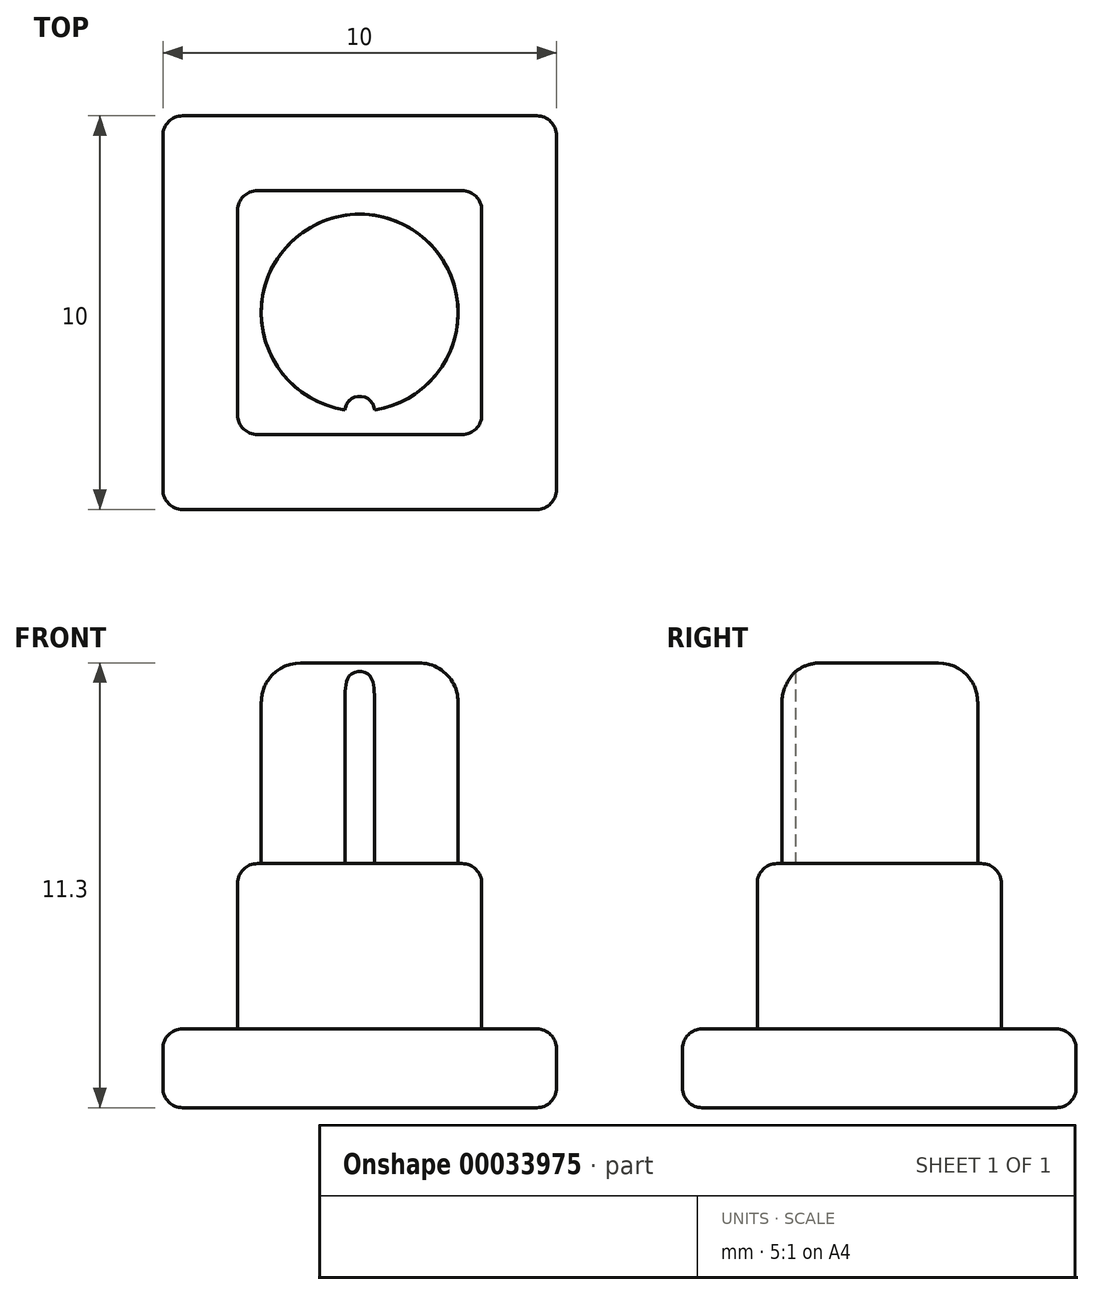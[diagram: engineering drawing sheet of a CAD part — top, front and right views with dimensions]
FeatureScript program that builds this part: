
annotation { "Feature Type Name" : "Feature", "Feature Type Description" : "" }
export const myFeature = defineFeature(function(context is Context, id is Id, definition is map)
    precondition{}
    {
        {
            var Q0;
            Q0=qCreatedBy(makeId("Top.planeOp"),FACE);
            var sketch = newSketch(context, id + "F0", { "sketchPlane" : qUnion([Q0])});
            skLineSegment(sketch, "E0.rect.bottom", {"start": v(3.1, -3.1) * mm, "end": v(-3.1, -3.1) * mm});
            skLineSegment(sketch, "E0.rect.top", {"start": v(3.1, 3.1) * mm, "end": v(-3.1, 3.1) * mm});
            skLineSegment(sketch, "E0.rect.left", {"start": v(3.1, -3.1) * mm, "end": v(3.1, 3.1) * mm});
            skLineSegment(sketch, "E0.rect.right", {"start": v(-3.1, -3.1) * mm, "end": v(-3.1, 3.1) * mm});
            skPoint(sketch, "E0.rect.middle", {"position": v(0, 0) * mm});
            skLineSegment(sketch, "E1.rect.bottom", {"start": v(5, -5) * mm, "end": v(-5, -5) * mm});
            skLineSegment(sketch, "E1.rect.top", {"start": v(5, 5) * mm, "end": v(-5, 5) * mm});
            skLineSegment(sketch, "E1.rect.left", {"start": v(5, -5) * mm, "end": v(5, 5) * mm});
            skLineSegment(sketch, "E1.rect.right", {"start": v(-5, -5) * mm, "end": v(-5, 5) * mm});
            skSolve(sketch);
        }
        {
            var Q0;
            Q0=makeQuery(id+"F0.imprint","IMPRINT",FACE,{"disambiguationData":[TD([[makeQuery(id+"F0.imprint","IMPRINT",EDGE,{"derivedFrom":sQuery(id+"F0.wireOp",EDGE,"E0.rect.bottom")}),-1.0]])]});
            extrude(context, id + "F1", {"entities" : qUnion([Q0]), "depth" : 6.2 * mm});
        }
        {
            var Q0;
            Q0=makeQuery(id+"F0.imprint","IMPRINT",FACE,{"disambiguationData":[TD([[makeQuery(id+"F0.imprint","IMPRINT",EDGE,{"derivedFrom":sQuery(id+"F0.wireOp",EDGE,"E0.rect.bottom")}),1.0]])]});
            var Q1;
            Q1=makeQuery(id+"F0.imprint","IMPRINT",FACE,{"disambiguationData":[TD([[makeQuery(id+"F0.imprint","IMPRINT",EDGE,{"derivedFrom":sQuery(id+"F0.wireOp",EDGE,"E0.rect.bottom")}),-1.0]])]});
            extrude(context, id + "F2", {"entities" : qUnion([Q0, Q1]), "operationType" : NewBodyOperationType.ADD, "depth" : 2 * mm});
        }
        {
            var Q0;
            Q0=makeQuery(id+"F1.opExtrude","CAP_FACE",FACE,{"disambiguationData":[OSD([sQuery(id+"F0.wireOp",EDGE,"E0.rect.bottom"),sQuery(id+"F0.wireOp",EDGE,"E0.rect.top"),sQuery(id+"F0.wireOp",EDGE,"E0.rect.left"),sQuery(id+"F0.wireOp",EDGE,"E0.rect.right")])],"isStart":false});
            var sketch = newSketch(context, id + "F3", { "sketchPlane" : qUnion([Q0])});
            skCircle(sketch, "E2", {"center": v(0, 0) * mm, "radius": 2.5 * mm});
            skCircle(sketch, "E3", {"center": v(0, 0) * mm, "radius": 1.75 * mm});
            skSolve(sketch);
        }
        {
            var Q0;
            Q0=makeQuery(id+"F3.imprint","IMPRINT",FACE,{"disambiguationData":[TD([[makeQuery(id+"F3.imprint","IMPRINT",EDGE,{"derivedFrom":sQuery(id+"F3.wireOp",EDGE,"E3")}),-1.0]])]});
            var Q1;
            Q1=makeQuery(id+"F3.imprint","IMPRINT",FACE,{"disambiguationData":[TD([[makeQuery(id+"F3.imprint","IMPRINT",EDGE,{"derivedFrom":sQuery(id+"F3.wireOp",EDGE,"E3")}),1.0]])]});
            extrude(context, id + "F4", {"entities" : qUnion([Q0, Q1]), "operationType" : NewBodyOperationType.ADD, "depth" : 5.1 * mm});
        }
        {
            var Q0;
            {var subQ0=sQuery(id+"F0.wireOp",EDGE,"E0.rect.bottom");var subQ1=sQuery(id+"F0.wireOp",EDGE,"E0.rect.left");var subQ2=makeQuery(id+"F1.opExtrude","CAP_FACE",FACE,{"disambiguationData":[OSD([subQ0,sQuery(id+"F0.wireOp",EDGE,"E0.rect.top"),subQ1,sQuery(id+"F0.wireOp",EDGE,"E0.rect.right")])],"isStart":false});Q0=makeQuery(id+"F4.boolean.opBoolean","SPLIT",FACE,{"disambiguationData":[TD([makeQuery(id+"F1.opExtrude","SWEPT_FACE",FACE,{"disambiguationData":[OSD([subQ0])]}),subQ2,makeQuery(id+"F1.opExtrude","SWEPT_FACE",FACE,{"disambiguationData":[OSD([subQ1])]}),makeQuery(id+"F4.opExtrude","SWEPT_FACE",FACE,{"disambiguationData":[OSD([sQuery(id+"F3.wireOp",EDGE,"E2")])]})])],"derivedFrom":subQ2});}
            var sketch = newSketch(context, id + "F5", { "sketchPlane" : qUnion([Q0])});
            skLineSegment(sketch, "E4.rect.bottom", {"start": v(8.04, -0.37) * mm, "end": v(-8.04, -0.38) * mm});
            skLineSegment(sketch, "E4.rect.top", {"start": v(8.04, 0.38) * mm, "end": v(-8.04, 0.37) * mm});
            skLineSegment(sketch, "E4.rect.left", {"start": v(8.04, -0.37) * mm, "end": v(8.04, 0.38) * mm});
            skLineSegment(sketch, "E4.rect.right", {"start": v(-8.04, -0.38) * mm, "end": v(-8.04, 0.37) * mm});
            skPoint(sketch, "E4.rect.middle", {"position": v(0, 0) * mm});
            skLineSegment(sketch, "E5.rect.bottom", {"start": v(-0.38, 7.54) * mm, "end": v(0.38, 7.54) * mm});
            skLineSegment(sketch, "E5.rect.top", {"start": v(-0.38, -7.54) * mm, "end": v(0.37, -7.54) * mm});
            skLineSegment(sketch, "E5.rect.left", {"start": v(-0.38, 7.54) * mm, "end": v(-0.38, -7.54) * mm});
            skLineSegment(sketch, "E5.rect.right", {"start": v(0.38, 7.54) * mm, "end": v(0.37, -7.54) * mm});
            skCircle(sketch, "E6", {"center": v(0, -2.5) * mm, "radius": 0.38 * mm});
            skSolve(sketch);
        }
        {
            var Q0;
            {var subQ0=makeQuery(id+"F4.opExtrude","CAP_EDGE",EDGE,{"disambiguationData":[OSD([sQuery(id+"F3.wireOp",EDGE,"E2")])],"isStart":true});var subQ1=sQuery(id+"F5.wireOp",EDGE,"E6");var subQ3=makeQuery(id+"F5.imprint","INTERSECT",VERTEX,{"disambiguationData":[OD(0.0)],"derivedFrom":[subQ0,subQ1]});Q0=makeQuery(id+"F5.imprint","IMPRINT",FACE,{"disambiguationData":[TD([[makeQuery(id+"F5.imprint","IMPRINT",EDGE,{"disambiguationData":[TD([[subQ3,-1.0]])],"derivedFrom":subQ1}),1.0]])]});}
            var Q1;
            {var subQ1=sQuery(id+"F5.wireOp",EDGE,"E6");var subQ3=sQuery(id+"F5.wireOp",EDGE,"E5.rect.left");var subQ5=makeQuery(id+"F5.imprint","INTERSECT",VERTEX,{"derivedFrom":[subQ3,subQ1]});Q1=makeQuery(id+"F5.imprint","IMPRINT",FACE,{"disambiguationData":[TD([[makeQuery(id+"F5.imprint","IMPRINT",EDGE,{"disambiguationData":[TD([[subQ5,1.0]])],"derivedFrom":subQ3}),1.0]])]});}
            extrude(context, id + "F6", {"entities" : qUnion([Q0, Q1]), "operationType" : NewBodyOperationType.REMOVE, "depth" : 25 * mm});
        }
        {
            var Q0;
            Q0=makeQuery(id+"F2.opExtrude","SWEPT_FACE",FACE,{"disambiguationData":[OSD([sQuery(id+"F0.wireOp",EDGE,"E1.rect.bottom")])]});
            var Q1;
            Q1=makeQuery(id+"F2.opExtrude","SWEPT_FACE",FACE,{"disambiguationData":[OSD([sQuery(id+"F0.wireOp",EDGE,"E1.rect.left")])]});
            var Q2;
            Q2=makeQuery(id+"F1.opExtrude","SWEPT_EDGE",EDGE,{"disambiguationData":[OSD([sQuery(id+"F0.wireOp",EDGE,"E0.rect.bottom"),sQuery(id+"F0.wireOp",EDGE,"E0.rect.left")])]});
            var Q3;
            {var subQ0=sQuery(id+"F0.wireOp",EDGE,"E0.rect.bottom");var subQ1=makeQuery(id+"F1.opExtrude","CAP_EDGE",EDGE,{"disambiguationData":[OSD([subQ0])],"isStart":false});var subQ3=sQuery(id+"F0.wireOp",EDGE,"E0.rect.left");var subQ4=sQuery(id+"F0.wireOp",EDGE,"E0.rect.right");Q3=makeQuery(id+"F6.boolean.opBoolean","MERGE",EDGE,{"derivedFrom":[makeQuery(id+"F4.boolean.opBoolean","SPLIT",EDGE,{"disambiguationData":[TD([makeQuery(id+"F1.opExtrude","SWEPT_FACE",FACE,{"disambiguationData":[OSD([subQ3])]})])],"derivedFrom":subQ1}),makeQuery(id+"F4.boolean.opBoolean","SPLIT",EDGE,{"disambiguationData":[TD([makeQuery(id+"F1.opExtrude","SWEPT_FACE",FACE,{"disambiguationData":[OSD([subQ4])]})])],"derivedFrom":subQ1})]});}
            var Q4;
            {var subQ0=sQuery(id+"F0.wireOp",EDGE,"E0.rect.left");var subQ1=makeQuery(id+"F1.opExtrude","CAP_EDGE",EDGE,{"disambiguationData":[OSD([subQ0])],"isStart":false});var subQ4=sQuery(id+"F0.wireOp",EDGE,"E0.rect.bottom");var subQ5=sQuery(id+"F0.wireOp",EDGE,"E0.rect.top");Q4=makeQuery(id+"F6.boolean.opBoolean","MERGE",EDGE,{"derivedFrom":[makeQuery(id+"F4.boolean.opBoolean","SPLIT",EDGE,{"disambiguationData":[TD([makeQuery(id+"F1.opExtrude","SWEPT_FACE",FACE,{"disambiguationData":[OSD([subQ4])]})])],"derivedFrom":subQ1}),makeQuery(id+"F4.boolean.opBoolean","SPLIT",EDGE,{"disambiguationData":[TD([makeQuery(id+"F1.opExtrude","SWEPT_FACE",FACE,{"disambiguationData":[OSD([subQ5])]})])],"derivedFrom":subQ1})]});}
            var Q5;
            Q5=makeQuery(id+"F1.opExtrude","SWEPT_EDGE",EDGE,{"disambiguationData":[OSD([sQuery(id+"F0.wireOp",EDGE,"E0.rect.bottom"),sQuery(id+"F0.wireOp",EDGE,"E0.rect.right")])]});
            var Q6;
            Q6=makeQuery(id+"F2.opExtrude","SWEPT_FACE",FACE,{"disambiguationData":[OSD([sQuery(id+"F0.wireOp",EDGE,"E1.rect.right")])]});
            var Q7;
            {var subQ0=sQuery(id+"F0.wireOp",EDGE,"E0.rect.right");var subQ1=makeQuery(id+"F1.opExtrude","CAP_EDGE",EDGE,{"disambiguationData":[OSD([subQ0])],"isStart":false});var subQ4=sQuery(id+"F0.wireOp",EDGE,"E0.rect.bottom");var subQ5=sQuery(id+"F0.wireOp",EDGE,"E0.rect.top");Q7=makeQuery(id+"F6.boolean.opBoolean","MERGE",EDGE,{"derivedFrom":[makeQuery(id+"F4.boolean.opBoolean","SPLIT",EDGE,{"disambiguationData":[TD([makeQuery(id+"F1.opExtrude","SWEPT_FACE",FACE,{"disambiguationData":[OSD([subQ4])]})])],"derivedFrom":subQ1}),makeQuery(id+"F4.boolean.opBoolean","SPLIT",EDGE,{"disambiguationData":[TD([makeQuery(id+"F1.opExtrude","SWEPT_FACE",FACE,{"disambiguationData":[OSD([subQ5])]})])],"derivedFrom":subQ1})]});}
            var Q8;
            Q8=makeQuery(id+"F1.opExtrude","SWEPT_EDGE",EDGE,{"disambiguationData":[OSD([sQuery(id+"F0.wireOp",EDGE,"E0.rect.top"),sQuery(id+"F0.wireOp",EDGE,"E0.rect.right")])]});
            var Q9;
            Q9=makeQuery(id+"F2.opExtrude","SWEPT_FACE",FACE,{"disambiguationData":[OSD([sQuery(id+"F0.wireOp",EDGE,"E1.rect.top")])]});
            var Q10;
            Q10=makeQuery(id+"F1.opExtrude","SWEPT_EDGE",EDGE,{"disambiguationData":[OSD([sQuery(id+"F0.wireOp",EDGE,"E0.rect.top"),sQuery(id+"F0.wireOp",EDGE,"E0.rect.left")])]});
            var Q11;
            {var subQ0=sQuery(id+"F0.wireOp",EDGE,"E0.rect.top");var subQ1=makeQuery(id+"F1.opExtrude","CAP_EDGE",EDGE,{"disambiguationData":[OSD([subQ0])],"isStart":false});var subQ3=sQuery(id+"F0.wireOp",EDGE,"E0.rect.left");var subQ5=sQuery(id+"F0.wireOp",EDGE,"E0.rect.right");Q11=makeQuery(id+"F6.boolean.opBoolean","MERGE",EDGE,{"derivedFrom":[makeQuery(id+"F4.boolean.opBoolean","SPLIT",EDGE,{"disambiguationData":[TD([makeQuery(id+"F1.opExtrude","SWEPT_FACE",FACE,{"disambiguationData":[OSD([subQ3])]})])],"derivedFrom":subQ1}),makeQuery(id+"F4.boolean.opBoolean","SPLIT",EDGE,{"disambiguationData":[TD([makeQuery(id+"F1.opExtrude","SWEPT_FACE",FACE,{"disambiguationData":[OSD([subQ5])]})])],"derivedFrom":subQ1})]});}
            fillet(context, id + "F7", {"entities" : qUnion([Q0, Q1, Q2, Q3, Q4, Q5, Q6, Q7, Q8, Q9, Q10, Q11]), "radius" : 0.5 * mm, "tangentPropagation" : true, "allowEdgeOverflow" : false});
        }
        {
            var Q0;
            Q0=makeQuery(id+"F4.opExtrude","CAP_EDGE",EDGE,{"disambiguationData":[OSD([sQuery(id+"F3.wireOp",EDGE,"E2")])],"isStart":false});
            fillet(context, id + "F8", {"entities" : qUnion([Q0]), "radius" : 1 * mm, "tangentPropagation" : true, "allowEdgeOverflow" : false});
        }
    });
